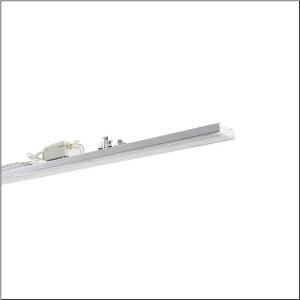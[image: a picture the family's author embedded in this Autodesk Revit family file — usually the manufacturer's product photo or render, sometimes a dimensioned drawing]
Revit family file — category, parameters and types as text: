
# Revit family: licross_r__21_recessed_ho_52te18dv4l2m_7c7f
name_source: partatom
category: Lighting Fixtures
units: mm (PartAtom-declared; Revit-internal decimal feet)

## family parameters
Cut with Voids When Loaded = No
Host = Face
Light Source = No
Part Type = Normal
Room Calculation Point = No
Round Connector Dimension = Use Diameter
Shared = No

## types (1)
- --- (1 x LED, 22480 lm, 125.6 W, 4000K)
    Apparent Load = 126 VA
    CIE Flux Codes = 75 94 99 100 100
    Color Rendering = 80
    Color Temperature = 4000K
    Default Elevation = 1800 mm
    Description = Licross® 21 Recessed HO, luminaire insert, of sheet steel, galvanised, coil coated, white, length: 2.250mm, width: 66mm, height: 67mm, LED rated luminous flux: 22.480lm, light colour: 840, control gear: DALI 2, with plug, 5-pole, with phase selection, mains connection: 220..240V, AC, 50/60Hz, rated input power: 126W, halogen-free wiring, primary light control with lens, of plastic, primary optical cover: cover, of PMMA, light emission: direct distribution, primary light characteristic: symmetric, protection rating (complete): IP54, insulation class (complete): insulation class I (protective earthing), certification: CE, ENEC, VDE, UKCA, protection symbol: D if used in an environment with non-conductive dust loads with corresponding accessories, impact resistance: IK06, permissible ambient temperature for indoor applications: -40..+30°C, corresponds to IFS (International Featured Standards) requirements for safety and quality in the food industry, reducing of maximum allowable ambient temperature of 5°C with ceiling mounting, LABS conformity tested according to VDMA 24364:2018-05, packaging unit: 1 piece
    Height = 58 mm
    Lamp = 1 x LED
    Lamp Light Flux = 22480 lm
    Lamp Power = 125.6 W
    Lamp count = 1
    Length = 2250 mm
    Luminous efficacy = 179 lm/W
    Manufacturer = Siteco
    ModVariant = No
    Model = 52TE18DV4L2M
    Mounting Place = Ceiling
    Mounting Type = Pendant
    Number of Poles = 1
    OnlyDefault = Yes
    Power Factor = 1
    Product Name = Licross® 21 Recessed HO
    Product group = luminaire insert
    ProductGroupID = 901
    Protection Class = Protection class I
    Protection Degree = IP 54
    RLX_Detail_Level = 1
    RLX_Emergency_Light_Flux = 0 lm
    RLX_Emergency_Type = 0
    RLX_Emergency_Type_DB = No
    RlxData = <blob elided: 29821 chars, md5=75f0a7d8>
    Socket = socket
    Standby Power = 0 W
    System Light Flux = 22480 lm
    System Power = 126 W
    Type Comments = factory setting: luminous flux: 100 % | dim-lin: 254 | 489 mA
    Type Image = l_1296930.jpg
    URL = http://relux.com
    VarID = @adj_057329
    Voltage = 0 V
    Weight = 0.00 kg
    Width = 66 mm

## geometry (parser evidence)
native form markers: Blend x4, Sweep x9
no freeform markers — native parametric forms only
